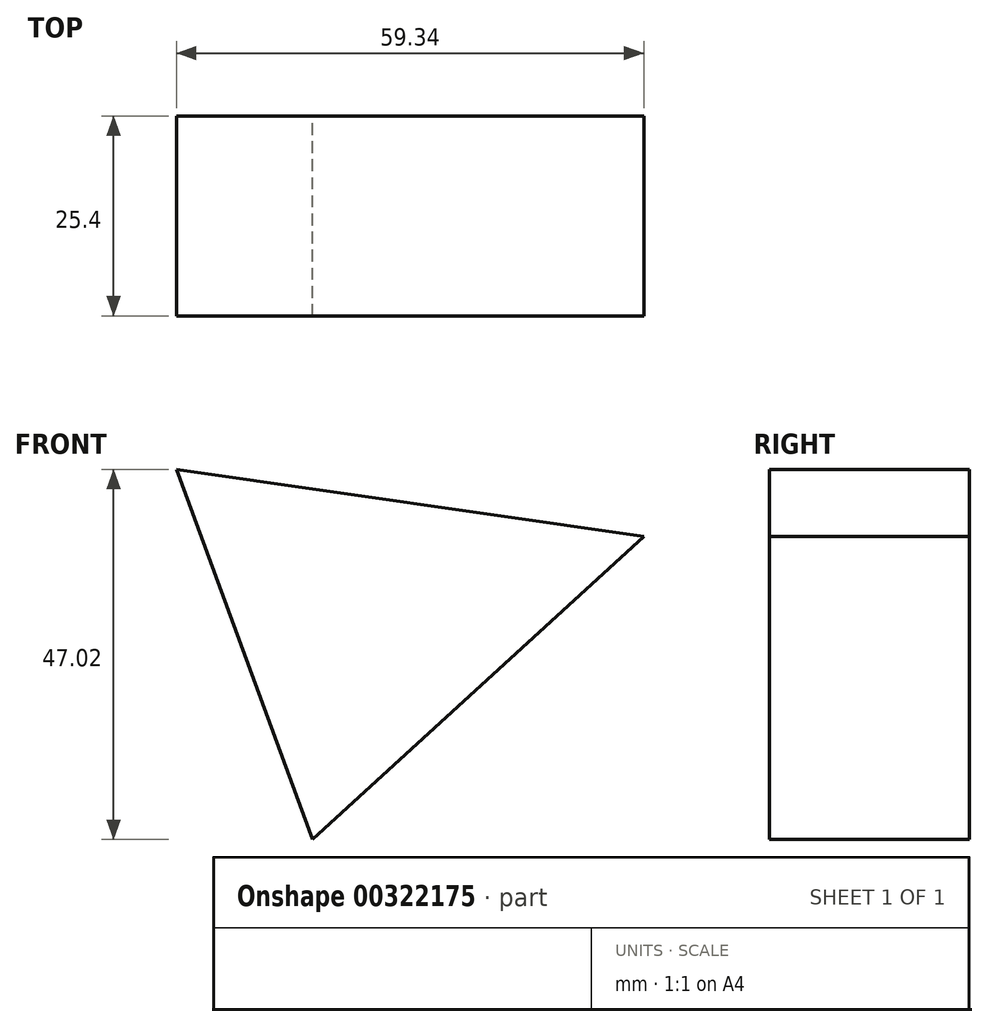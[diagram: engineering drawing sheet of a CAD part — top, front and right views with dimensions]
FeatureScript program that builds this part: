
annotation { "Feature Type Name" : "Feature", "Feature Type Description" : "" }
export const myFeature = defineFeature(function(context is Context, id is Id, definition is map)
    precondition{}
    {
        {
            var Q0;
            Q0=qCreatedBy(makeId("Front.planeOp"),FACE);
            var sketch = newSketch(context, id + "F0", { "sketchPlane" : qUnion([Q0])});
            skLineSegment(sketch, "E0", {"start": v(0, 0) * mm, "end": v(42.1, 38.49) * mm});
            skLineSegment(sketch, "E1", {"start": v(42.1, 38.49) * mm, "end": v(-17.25, 47.02) * mm});
            skLineSegment(sketch, "E2", {"start": v(-17.25, 47.02) * mm, "end": v(0, 0) * mm});
            skSolve(sketch);
        }
        {
            var Q0;
            Q0 = qSketchRegion(id + "F0", true);
            extrude(context, id + "F1", {"entities" : qUnion([Q0]), "depth" : 25.4 * mm});
        }
    });
